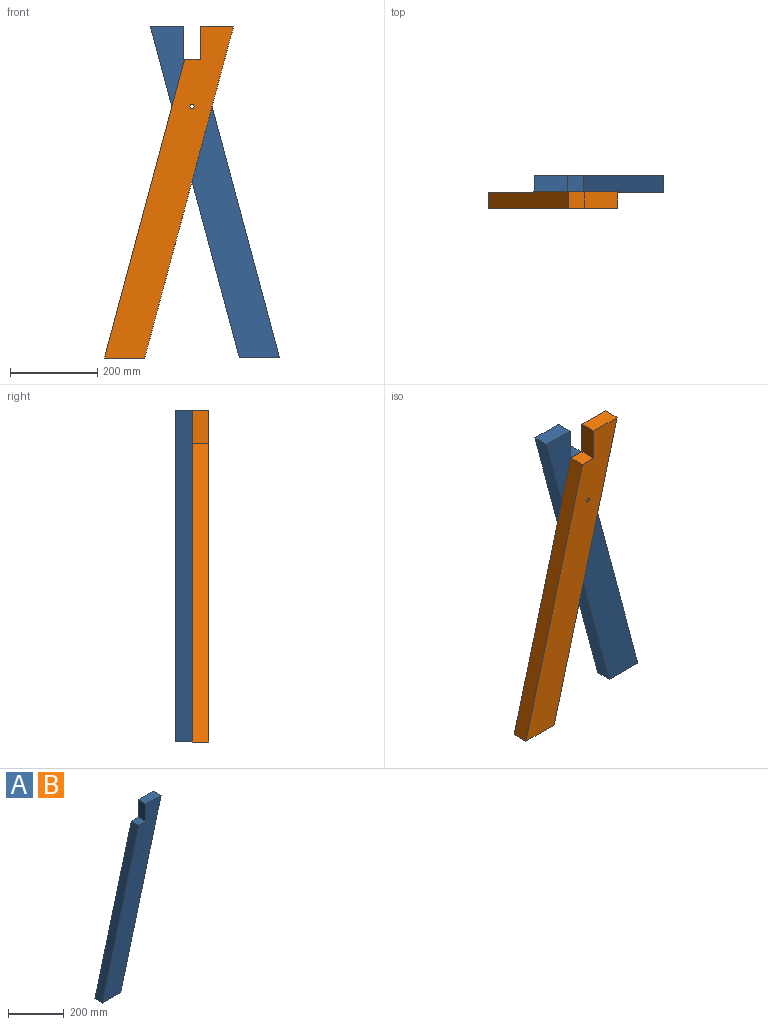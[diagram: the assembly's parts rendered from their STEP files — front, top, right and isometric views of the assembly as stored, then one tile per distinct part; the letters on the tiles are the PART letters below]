
ASSEMBLY  parts=2 mates=1
PART A: 9 faces, bbox 295.8x38.1x760.6 mm
  f0: plane 38.1x36.25mm, normal (0,0,1), area 1381.3mm2, adj f1,f6,f7,f8
  f1: plane 684.37x183.38mm, normal (-0.97,0,0.26), area 26994.3mm2, adj f0,f2,f7,f8
  f2: plane 92.04x38.1mm, normal (0,0,-1), area 3506.6mm2, adj f1,f3,f7,f8
  f3: plane 760.57x203.79mm, normal (0.97,0,-0.26), area 29999.9mm2, adj f2,f4,f7,f8
  f4: plane 76.2x38.1mm, normal (0,0,1), area 2903.2mm2, adj f3,f6,f7,f8
  f5: cylinder r=4.76mm len=38.1mm, axis (0,1,0), area 1140.1mm2, adj f7,f8
  f6: plane 76.2x38.1mm, normal (-1,0,0), area 2903.2mm2, adj f0,f4,f7,f8
  f7: plane 760.57x295.83mm, normal (0,-1,0), area 67944mm2, adj f0,f1,f2,f3,f4,f5,f6
  f8: plane 760.57x295.83mm, normal (0,1,0), area 67944mm2, adj f0,f1,f2,f3,f4,f5,f6
PART B: same geometry as A
PLACE A rot(axis=(0,0,1),180deg) t=(209.49,31.36,258.55)mm
PLACE B t=(177.66,31.36,258.55)mm
MATE revolute A.f5 <-> B.f5  axis (0,-1,0) through (193.58,31.36,563.34)mm
